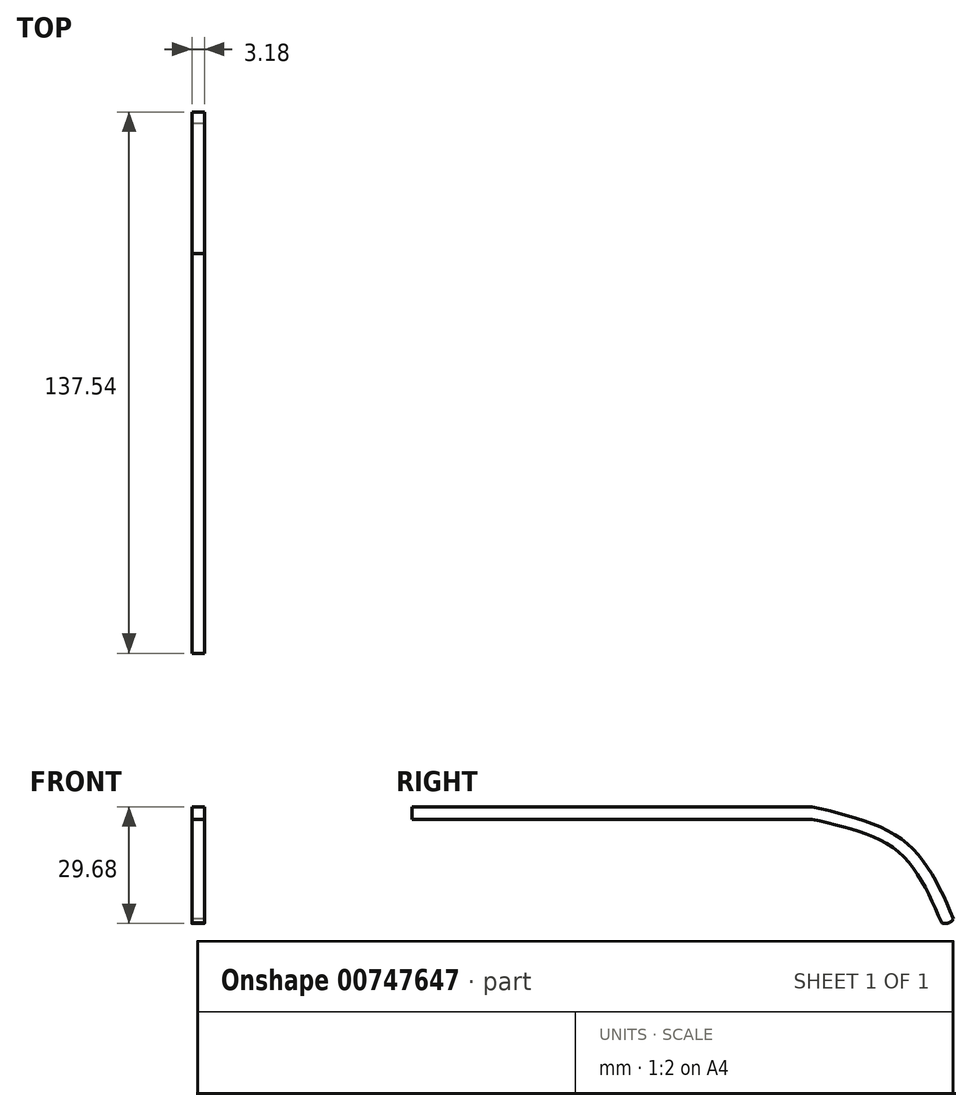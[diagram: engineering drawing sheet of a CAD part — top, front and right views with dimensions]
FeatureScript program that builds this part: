
annotation { "Feature Type Name" : "Feature", "Feature Type Description" : "" }
export const myFeature = defineFeature(function(context is Context, id is Id, definition is map)
    precondition{}
    {
        {
            var Q0;
            Q0=qCreatedBy(makeId("Right.planeOp"),FACE);
            var sketch = newSketch(context, id + "F0", { "sketchPlane" : qUnion([Q0])});
            skLineSegment(sketch, "E0", {"start": v(-69.23, 46.5) * mm, "end": v(32.37, 46.5) * mm});
            skLineSegment(sketch, "E1", {"start": v(-69.23, 46.5) * mm, "end": v(-69.23, 43.32) * mm});
            skLineSegment(sketch, "E2", {"start": v(-69.23, 43.32) * mm, "end": v(32.37, 43.32) * mm});
            skFitSpline(sketch, "E3", {"points": [v(32.37, 46.5) * mm, v(56.41, 37.26) * mm, v(68.3, 18.07) * mm], "startDerivative": vector(53.6, -12.27) * mm, "endDerivative": vector(19.78, -45.61) * mm});
            skFitSpline(sketch, "E4", {"points": [v(32.37, 43.32) * mm, v(53.83, 35.41) * mm, v(65.32, 17) * mm], "startDerivative": vector(45.78, -10.28) * mm, "endDerivative": vector(18.17, -41.98) * mm});
            skArc(sketch, "E5", {"start": v(65.32, 17) * mm, "mid": v(67.02, 16.96) * mm, "end": v(68.3, 18.07) * mm});
            skSolve(sketch);
        }
        {
            var Q0;
            Q0=makeQuery(id+"F0.imprint","IMPRINT",FACE,{"disambiguationData":[TD([[makeQuery(id+"F0.imprint","IMPRINT",EDGE,{"derivedFrom":sQuery(id+"F0.wireOp",EDGE,"E0")}),-1.0]])]});
            extrude(context, id + "F1", {"entities" : qUnion([Q0]), "depth" : 3.17 * mm, "offsetDistance" : 25.4 * mm});
        }
    });
